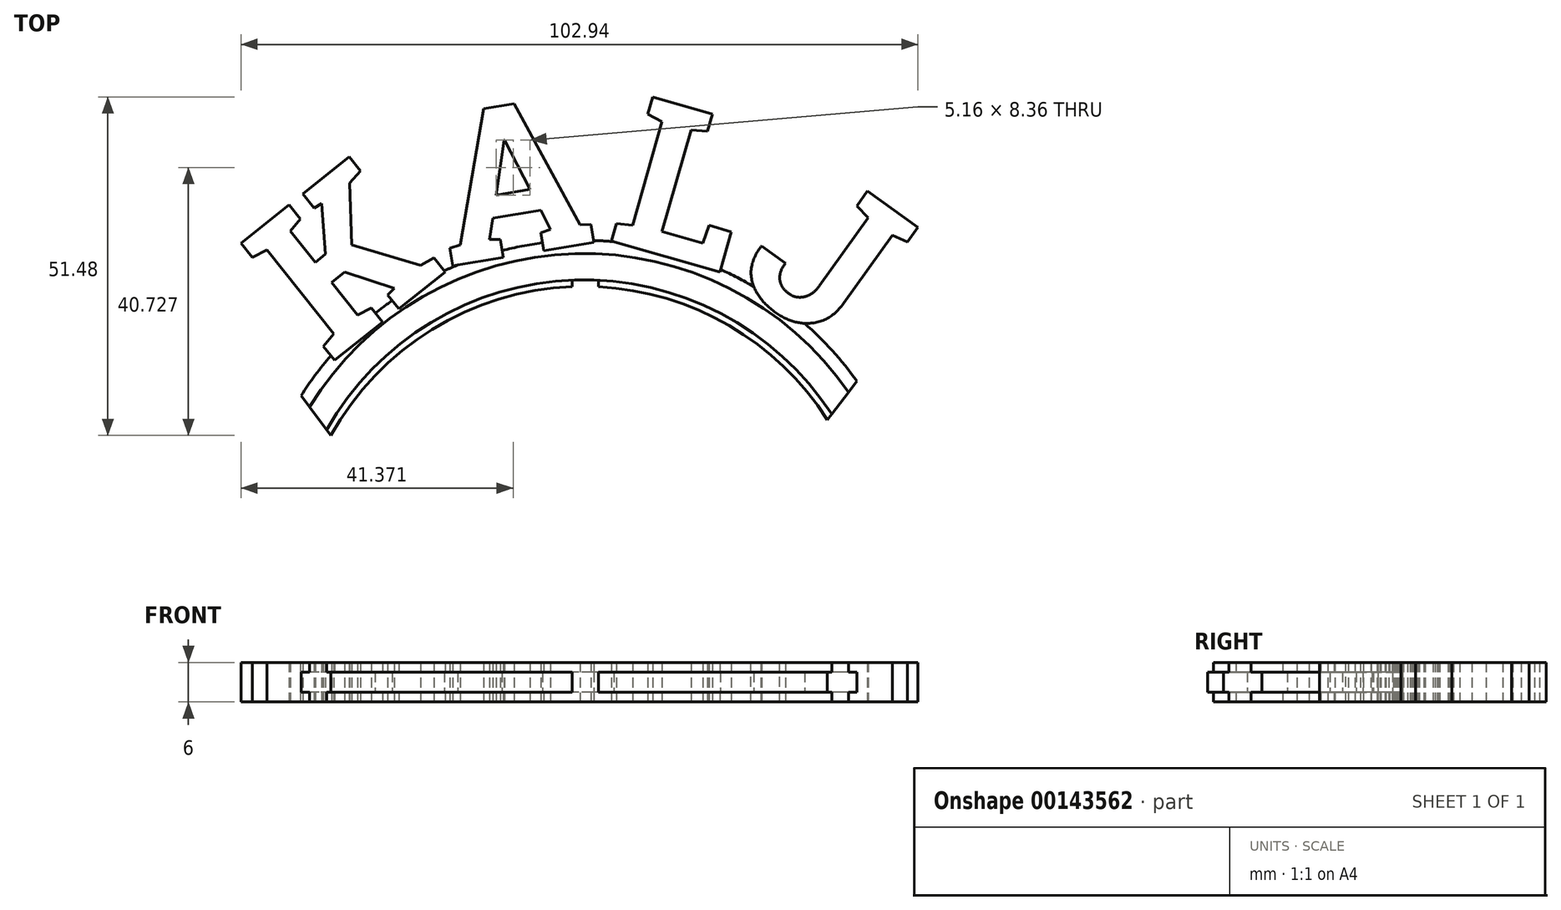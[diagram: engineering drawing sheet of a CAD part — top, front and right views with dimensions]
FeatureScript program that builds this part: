
annotation { "Feature Type Name" : "Feature", "Feature Type Description" : "" }
export const myFeature = defineFeature(function(context is Context, id is Id, definition is map)
    precondition{}
    {
        {
            var Q0;
            Q0=qCreatedBy(makeId("Top.planeOp"),FACE);
            var sketch = newSketch(context, id + "F0", { "sketchPlane" : qUnion([Q0])});
            skCircle(sketch, "E0", {"center": v(0, 0) * mm, "radius": 50 * mm, "construction": true});
            skText(sketch, "E1", { "text": "L", "fontName": "RobotoSlab-Bold.ttf"});
            skText(sketch, "E2", { "text": "K", "fontName": "RobotoSlab-Bold.ttf"});
            skText(sketch, "E3", { "text": "A", "fontName": "RobotoSlab-Bold.ttf"});
            skText(sketch, "E4", { "text": "J", "fontName": "RobotoSlab-Bold.ttf"});
            skArc(sketch, "E5.0", {"start": v(37.7, 24.57) * mm, "mid": v(-1.38, 44.98) * mm, "end": v(-39.13, 22.22) * mm});
            skLineSegment(sketch, "E6", {"start": v(0, 0) * mm, "end": v(-41.65, 55.6) * mm, "construction": true});
            skLineSegment(sketch, "E7", {"start": v(0, 0) * mm, "end": v(44.37, 57.96) * mm, "construction": true});
            skLineSegment(sketch, "E8.0", {"start": v(37.05, 23.73) * mm, "end": v(59.68, 53.28) * mm});
            skLineSegment(sketch, "E9.0", {"start": v(-38.48, 21.34) * mm, "end": v(-61.14, 51.6) * mm});
            skArc(sketch, "E10.0", {"start": v(37.05, 23.73) * mm, "mid": v(22.09, 38.05) * mm, "end": v(2.23, 43.94) * mm});
            skLineSegment(sketch, "E11", {"start": v(0.23, 44) * mm, "end": v(0.23, 45) * mm, "construction": true});
            skLineSegment(sketch, "E12.0", {"start": v(-1.77, 43.96) * mm, "end": v(-1.77, 44.97) * mm});
            skLineSegment(sketch, "E13.0", {"start": v(2.23, 43.94) * mm, "end": v(2.23, 44.94) * mm});
            skArc(sketch, "E14.trimOffspring", {"start": v(-1.77, 43.96) * mm, "mid": v(-23.09, 37.46) * mm, "end": v(-38.48, 21.34) * mm});
            skArc(sketch, "E15.0", {"start": v(42.73, 27.85) * mm, "mid": v(-1.56, 50.98) * mm, "end": v(-44.35, 25.18) * mm});
            skArc(sketch, "E16.0", {"start": v(41.05, 26.76) * mm, "mid": v(-1.5, 48.98) * mm, "end": v(-42.61, 24.2) * mm});
            const initialGuessF0  = {"E1": [0.00335, 0.05114, 0.9615, -0.27482, 0.02309], "E2": [-0.0386, 0.03222, 0.7817, 0.62364, 0.02309], "E3": [-0.02056, 0.04703, 0.98636, 0.16457, 0.02309], "E4": [0.0227, 0.04508, 0.8129, -0.5824, 0.02309]};
            skSetInitialGuess(sketch, initialGuessF0);
            skSolve(sketch);
        }
        {
            var Q0;
            {var subQ0=sQuery(id+"F0.wireOp",EDGE,"I7mUoY96-e34o-nxmB-pDM6-qLCe9GAv2hIS.right");var subQ1=sQuery(id+"F0.wireOp",EDGE,"E3.sketch_text.stroke-10");var subQ2=makeQuery(id+"F0.imprint","INTERSECT",VERTEX,{"derivedFrom":[subQ1,subQ0]});Q0=makeQuery(id+"F0.imprint","IMPRINT",FACE,{"disambiguationData":[TD([[makeQuery(id+"F0.imprint","IMPRINT",EDGE,{"disambiguationData":[TD([[subQ2,-1.0]])],"derivedFrom":subQ1}),-1.0]])]});}
            var Q1;
            {var subQ10=sQuery(id+"F0.wireOp",EDGE,"E2.sketch_text.stroke-0");Q1=makeQuery(id+"F0.imprint","IMPRINT",FACE,{"disambiguationData":[TD([[makeQuery(id+"F0.imprint","IMPRINT",EDGE,{"derivedFrom":subQ10}),-1.0]])]});}
            var Q2;
            {var subQ17=sQuery(id+"F0.wireOp",EDGE,"E3.sketch_text.stroke-4");Q2=makeQuery(id+"F0.imprint","IMPRINT",FACE,{"disambiguationData":[TD([[makeQuery(id+"F0.imprint","IMPRINT",EDGE,{"derivedFrom":subQ17}),-1.0]])]});}
            var Q3;
            Q3=makeQuery(id+"F0.imprint","IMPRINT",FACE,{"disambiguationData":[TD([[makeQuery(id+"F0.imprint","IMPRINT",EDGE,{"derivedFrom":sQuery(id+"F0.wireOp",EDGE,"E3.sketch_text.stroke-0")}),-1.0]])]});
            var Q4;
            {var subQ0=sQuery(id+"F0.wireOp",EDGE,"E3.sketch_text.stroke-18");Q4=makeQuery(id+"F0.imprint","IMPRINT",FACE,{"disambiguationData":[TD([[makeQuery(id+"F0.imprint","IMPRINT",EDGE,{"derivedFrom":subQ0}),-1.0]])]});}
            var Q5;
            {var subQ0=sQuery(id+"F0.wireOp",EDGE,"E1.sketch_text.stroke-0");Q5=makeQuery(id+"F0.imprint","IMPRINT",FACE,{"disambiguationData":[TD([[makeQuery(id+"F0.imprint","IMPRINT",EDGE,{"derivedFrom":subQ0}),-1.0]])]});}
            var Q6;
            Q6=makeQuery(id+"F0.imprint","IMPRINT",FACE,{"disambiguationData":[TD([[makeQuery(id+"F0.imprint","IMPRINT",EDGE,{"derivedFrom":sQuery(id+"F0.wireOp",EDGE,"E4.sketch_text.stroke-0")}),-1.0]])]});
            var Q7;
            {var subQ0=sQuery(id+"F0.wireOp",EDGE,"E2.sketch_text.stroke-27");Q7=makeQuery(id+"F0.imprint","IMPRINT",FACE,{"disambiguationData":[TD([[makeQuery(id+"F0.imprint","IMPRINT",EDGE,{"derivedFrom":subQ0}),-1.0]])]});}
            var Q8;
            {var subQ0=sQuery(id+"F0.wireOp",EDGE,"E2.sketch_text.stroke-19");Q8=makeQuery(id+"F0.imprint","IMPRINT",FACE,{"disambiguationData":[TD([[makeQuery(id+"F0.imprint","IMPRINT",EDGE,{"derivedFrom":subQ0}),-1.0]])]});}
            var Q9;
            {var subQ0=sQuery(id+"F0.wireOp",EDGE,"E3.sketch_text.stroke-14");var subQ1=sQuery(id+"F0.wireOp",EDGE,"E3.sketch_text.stroke-13");var subQ2=makeQuery(id+"F0.imprint","INTERSECT",VERTEX,{"derivedFrom":[subQ1,subQ0]});Q9=makeQuery(id+"F0.imprint","IMPRINT",FACE,{"disambiguationData":[TD([[makeQuery(id+"F0.imprint","IMPRINT",EDGE,{"disambiguationData":[TD([[subQ2,1.0]])],"derivedFrom":subQ1}),-1.0]])]});}
            var Q10;
            {var subQ0=sQuery(id+"F0.wireOp",EDGE,"E3.sketch_text.stroke-6");Q10=makeQuery(id+"F0.imprint","IMPRINT",FACE,{"disambiguationData":[TD([[makeQuery(id+"F0.imprint","IMPRINT",EDGE,{"derivedFrom":subQ0}),-1.0]])]});}
            var Q11;
            {var subQ0=sQuery(id+"F0.wireOp",EDGE,"E1.sketch_text.stroke-15");var subQ1=sQuery(id+"F0.wireOp",EDGE,"E1.sketch_text.stroke-14");var subQ2=makeQuery(id+"F0.imprint","INTERSECT",VERTEX,{"derivedFrom":[subQ1,subQ0]});Q11=makeQuery(id+"F0.imprint","IMPRINT",FACE,{"disambiguationData":[TD([[makeQuery(id+"F0.imprint","IMPRINT",EDGE,{"disambiguationData":[TD([[subQ2,1.0]])],"derivedFrom":subQ1}),-1.0]])]});}
            var Q12;
            {var subQ0=sQuery(id+"F0.wireOp",EDGE,"E4.sketch_text.stroke-5");var subQ1=sQuery(id+"F0.wireOp",EDGE,"E4.sketch_text.stroke-4");var subQ2=makeQuery(id+"F0.imprint","INTERSECT",VERTEX,{"derivedFrom":[subQ1,subQ0]});Q12=makeQuery(id+"F0.imprint","IMPRINT",FACE,{"disambiguationData":[TD([[makeQuery(id+"F0.imprint","IMPRINT",EDGE,{"disambiguationData":[TD([[subQ2,1.0]])],"derivedFrom":subQ1}),-1.0]])]});}
            var Q13;
            {var subQ0=sQuery(id+"F0.wireOp",EDGE,"E8.0");var subQ1=sQuery(id+"F0.wireOp",EDGE,"E5.0");var subQ2=makeQuery(id+"F0.imprint","INTERSECT",VERTEX,{"derivedFrom":[subQ1,subQ0]});Q13=makeQuery(id+"F0.imprint","IMPRINT",FACE,{"disambiguationData":[TD([[makeQuery(id+"F0.imprint","IMPRINT",EDGE,{"disambiguationData":[TD([[subQ2,-1.0]])],"derivedFrom":subQ1}),-1.0]])]});}
            extrude(context, id + "F1", {"entities" : qUnion([Q0, Q1, Q2, Q3, Q4, Q5, Q6, Q7, Q8, Q9, Q10, Q11, Q12, Q13]), "endBound" : BoundingType.SYMMETRIC, "depth" : 6 * mm});
        }
        {
            var Q0;
            {var subQ1=sQuery(id+"F0.wireOp",EDGE,"E3.sketch_text.stroke-5");var subQ7=sQuery(id+"F0.wireOp",EDGE,"E3.sketch_text.stroke-6");var subQ9=makeQuery(id+"F0.imprint","INTERSECT",VERTEX,{"derivedFrom":[subQ1,subQ7]});Q0=makeQuery(id+"F0.imprint","IMPRINT",FACE,{"disambiguationData":[TD([[makeQuery(id+"F0.imprint","IMPRINT",EDGE,{"disambiguationData":[TD([[subQ9,1.0]])],"derivedFrom":subQ1}),-1.0]])]});}
            var Q1;
            {var subQ0=sQuery(id+"F0.wireOp",EDGE,"E15.0");var subQ1=sQuery(id+"F0.wireOp",EDGE,"E3.sketch_text.stroke-13");var subQ2=makeQuery(id+"F0.imprint","INTERSECT",VERTEX,{"derivedFrom":[subQ1,subQ0]});Q1=makeQuery(id+"F0.imprint","IMPRINT",FACE,{"disambiguationData":[TD([[makeQuery(id+"F0.imprint","IMPRINT",EDGE,{"disambiguationData":[TD([[subQ2,-1.0]])],"derivedFrom":subQ1}),-1.0]])]});}
            var Q2;
            {var subQ1=sQuery(id+"F0.wireOp",EDGE,"E2.sketch_text.stroke-18");var subQ5=sQuery(id+"F0.wireOp",EDGE,"E2.sketch_text.stroke-19");var subQ6=makeQuery(id+"F0.imprint","INTERSECT",VERTEX,{"derivedFrom":[subQ1,subQ5]});Q2=makeQuery(id+"F0.imprint","IMPRINT",FACE,{"disambiguationData":[TD([[makeQuery(id+"F0.imprint","IMPRINT",EDGE,{"disambiguationData":[TD([[subQ6,1.0]])],"derivedFrom":subQ1}),1.0]])]});}
            var Q3;
            {var subQ5=sQuery(id+"F0.wireOp",EDGE,"E2.sketch_text.stroke-18");var subQ7=sQuery(id+"F0.wireOp",EDGE,"E2.sketch_text.stroke-19");var subQ8=makeQuery(id+"F0.imprint","INTERSECT",VERTEX,{"derivedFrom":[subQ5,subQ7]});Q3=makeQuery(id+"F0.imprint","IMPRINT",FACE,{"disambiguationData":[TD([[makeQuery(id+"F0.imprint","IMPRINT",EDGE,{"disambiguationData":[TD([[subQ8,1.0]])],"derivedFrom":subQ5}),-1.0]])]});}
            var Q4;
            {var subQ6=sQuery(id+"F0.wireOp",EDGE,"E1.sketch_text.stroke-14");var subQ11=sQuery(id+"F0.wireOp",EDGE,"E1.sketch_text.stroke-15");var subQ12=makeQuery(id+"F0.imprint","INTERSECT",VERTEX,{"derivedFrom":[subQ6,subQ11]});Q4=makeQuery(id+"F0.imprint","IMPRINT",FACE,{"disambiguationData":[TD([[makeQuery(id+"F0.imprint","IMPRINT",EDGE,{"disambiguationData":[TD([[subQ12,1.0]])],"derivedFrom":subQ6}),1.0]])]});}
            var Q5;
            {var subQ0=sQuery(id+"F0.wireOp",EDGE,"E1.sketch_text.stroke-15");var subQ1=sQuery(id+"F0.wireOp",EDGE,"E1.sketch_text.stroke-14");var subQ2=makeQuery(id+"F0.imprint","INTERSECT",VERTEX,{"derivedFrom":[subQ1,subQ0]});Q5=makeQuery(id+"F0.imprint","IMPRINT",FACE,{"disambiguationData":[TD([[makeQuery(id+"F0.imprint","IMPRINT",EDGE,{"disambiguationData":[TD([[subQ2,1.0]])],"derivedFrom":subQ1}),-1.0]])]});}
            var Q6;
            {var subQ3=sQuery(id+"F0.wireOp",EDGE,"E15.0");var subQ7=sQuery(id+"F0.wireOp",EDGE,"E2.sketch_text.stroke-26");var subQ8=makeQuery(id+"F0.imprint","INTERSECT",VERTEX,{"derivedFrom":[subQ7,subQ3]});Q6=makeQuery(id+"F0.imprint","IMPRINT",FACE,{"disambiguationData":[TD([[makeQuery(id+"F0.imprint","IMPRINT",EDGE,{"disambiguationData":[TD([[subQ8,-1.0]])],"derivedFrom":subQ7}),-1.0]])]});}
            var Q7;
            {var subQ0=sQuery(id+"F0.wireOp",EDGE,"E15.0");var subQ1=sQuery(id+"F0.wireOp",EDGE,"E4.sketch_text.stroke-4");var subQ2=makeQuery(id+"F0.imprint","INTERSECT",VERTEX,{"derivedFrom":[subQ1,subQ0]});Q7=makeQuery(id+"F0.imprint","IMPRINT",FACE,{"disambiguationData":[TD([[makeQuery(id+"F0.imprint","IMPRINT",EDGE,{"disambiguationData":[TD([[subQ2,-1.0]])],"derivedFrom":subQ1}),-1.0]])]});}
            var Q8;
            {var subQ0=sQuery(id+"F0.wireOp",EDGE,"E15.0");var subQ1=sQuery(id+"F0.wireOp",EDGE,"E4.sketch_text.stroke-4");var subQ2=makeQuery(id+"F0.imprint","INTERSECT",VERTEX,{"derivedFrom":[subQ1,subQ0]});Q8=makeQuery(id+"F0.imprint","IMPRINT",FACE,{"disambiguationData":[TD([[makeQuery(id+"F0.imprint","IMPRINT",EDGE,{"disambiguationData":[TD([[subQ2,-1.0]])],"derivedFrom":subQ1}),1.0]])]});}
            var Q9;
            {var subQ4=sQuery(id+"F0.wireOp",EDGE,"E10.0");Q9=makeQuery(id+"F0.imprint","IMPRINT",FACE,{"disambiguationData":[TD([[makeQuery(id+"F0.imprint","IMPRINT",EDGE,{"derivedFrom":subQ4}),-1.0]])]});}
            var Q10;
            {var subQ3=sQuery(id+"F0.wireOp",EDGE,"E12.0");Q10=makeQuery(id+"F0.imprint","IMPRINT",FACE,{"disambiguationData":[TD([[makeQuery(id+"F0.imprint","IMPRINT",EDGE,{"derivedFrom":subQ3}),1.0]])]});}
            var Q11;
            {var subQ5=sQuery(id+"F0.wireOp",EDGE,"E2.sketch_text.stroke-28");var subQ6=sQuery(id+"F0.wireOp",EDGE,"E2.sketch_text.stroke-27");var subQ7=makeQuery(id+"F0.imprint","INTERSECT",VERTEX,{"derivedFrom":[subQ6,subQ5]});Q11=makeQuery(id+"F0.imprint","IMPRINT",FACE,{"disambiguationData":[TD([[makeQuery(id+"F0.imprint","IMPRINT",EDGE,{"disambiguationData":[TD([[subQ7,1.0]])],"derivedFrom":subQ6}),1.0]])]});}
            extrude(context, id + "F2", {"entities" : qUnion([Q0, Q1, Q2, Q3, Q4, Q5, Q6, Q7, Q8, Q9, Q10, Q11]), "operationType" : NewBodyOperationType.ADD, "endBound" : BoundingType.SYMMETRIC, "depth" : 3 * mm});
        }
    });
